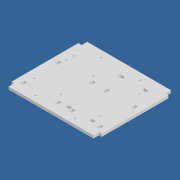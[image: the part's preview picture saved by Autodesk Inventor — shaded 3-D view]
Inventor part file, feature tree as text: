
AUTODESK INVENTOR PART (.ipt)
format: ipt  version: 2021 (Build 250183000, 183)  size: 232,960 bytes
history: native  units: mm
features: extrude x3, sketch x3, other x1
ambient origin geometry x8: Origin, YZ Plane, XZ Plane, XY Plane, X Axis, Y Axis, Z Axis, Center Point
bodies: Solid1 (feature_tree)
feature tree (7):
  other  "<userpath>\OneDrive\Objet3D\Clawd3\parameters.xlsx"
  extrude  "Extrusion1"  Depth=162.0mm
  extrude  "Extrusion2"  Depth=5.0mm
  extrude  "Extrusion3"  Depth=10.0mm
  sketch  "Sketch1"  dims[d0=120.0mm d1=162.0mm]
  sketch  "Sketch2"  dims[d2=5.0mm d3=5.0mm]
  sketch  "Sketch4"  dims[d4=10.0mm d5=10.0mm d6=150.0mm d7=5.0mm d8=0.0mm d9=3.0mm d10=15.0mm d11=58.0mm d12=49.0mm d13=49.0mm d14=58.0mm d15=3.0mm d16=3.0mm d17=3.088792mm d18=35.0mm d19=70.7mm d20=118.3mm d21=70.7mm d22=118.3mm d23=3.0mm d24=3.0mm d25=3.0mm d26=5.0mm d27=8.0mm d28=8.0mm d29=5.0mm d30=8.0mm d31=5.0mm d32=5.0mm d33=8.0mm d34=8.0mm d35=5.0mm d36=5.0mm d37=8.0mm d38=8.0mm d39=5.0mm d40=5.0mm d41=8.0mm d42=50.0mm d43=25.0mm d44=50.0mm d45=25.0mm d46=90.0mm d47=90.0mm d48=55.0mm d49=55.0mm d50=70.0mm d51=70.0mm d52=10.0mm d53=40.0mm d54=0.0mm d55=35.0mm d56=15.0mm d57=15.0mm d58=8.0mm d59=10.0mm d60=5.0mm d61=5.0mm d62=8.0mm d63=10.0mm d64=70.0mm d65=5.0mm d66=5.0mm d67=8.0mm d68=8.0mm d69=70.0mm d70=0.0mm d71=0.0mm d72=118.3mm d73=70.7mm d74=118.3mm d75=70.7mm d76=70.7mm d77=118.3mm d78=3.0mm d79=3.0mm d80=3.0mm d81=3.0mm d82=3.0mm d83=12.0mm d84=12.0mm d85=30.0mm d86=0.0mm]
